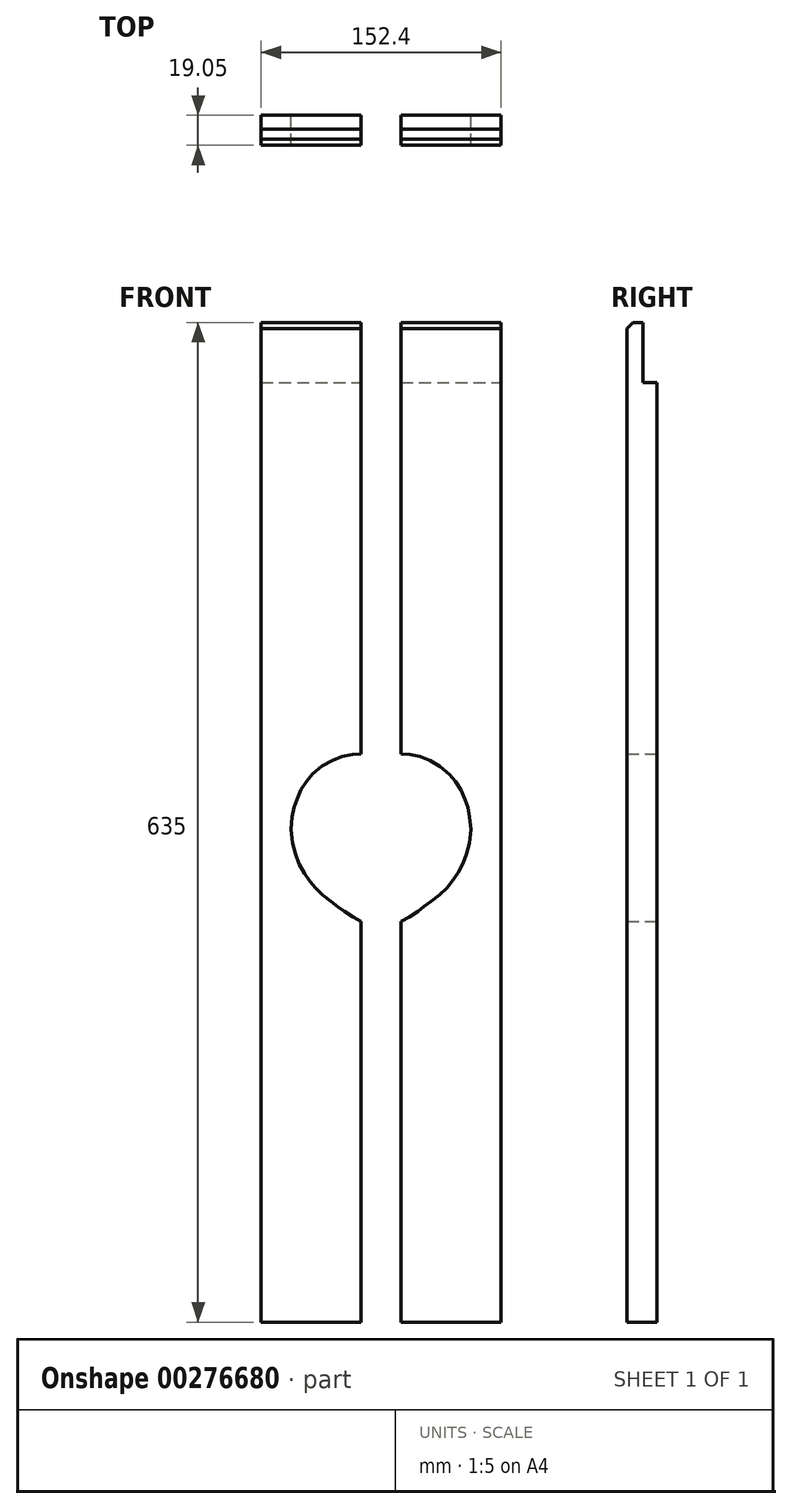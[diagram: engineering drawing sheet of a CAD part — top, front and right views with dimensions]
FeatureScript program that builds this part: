
annotation { "Feature Type Name" : "Feature", "Feature Type Description" : "" }
export const myFeature = defineFeature(function(context is Context, id is Id, definition is map)
    precondition{}
    {
        {
            var Q0;
            Q0=qCreatedBy(makeId("Front.planeOp"),FACE);
            var sketch = newSketch(context, id + "F0", { "sketchPlane" : qUnion([Q0])});
            skLineSegment(sketch, "E0.bottom", {"start": v(0, 0) * mm, "end": v(63.5, 0) * mm});
            skLineSegment(sketch, "E0.top", {"start": v(0, 635) * mm, "end": v(63.5, 635) * mm});
            skLineSegment(sketch, "E0.left", {"start": v(0, 0) * mm, "end": v(0, 635) * mm});
            skLineSegment(sketch, "E0.right", {"start": v(63.5, 0) * mm, "end": v(63.5, 635) * mm});
            skLineSegment(sketch, "E1.bottom", {"start": v(88.9, 0) * mm, "end": v(152.4, 0) * mm});
            skLineSegment(sketch, "E1.top", {"start": v(88.9, 635) * mm, "end": v(152.4, 635) * mm});
            skLineSegment(sketch, "E1.left", {"start": v(88.9, 0) * mm, "end": v(88.9, 635) * mm});
            skLineSegment(sketch, "E1.right", {"start": v(152.4, 0) * mm, "end": v(152.4, 635) * mm});
            skSolve(sketch);
        }
        {
            var Q0;
            Q0=makeQuery(id+"F0.imprint","IMPRINT",FACE,{"disambiguationData":[TD([[makeQuery(id+"F0.imprint","IMPRINT",EDGE,{"derivedFrom":sQuery(id+"F0.wireOp",EDGE,"E0.bottom")}),1.0]])]});
            extrude(context, id + "F1", {"entities" : qUnion([Q0]), "depth" : 19.05 * mm, "offsetDistance" : 25.4 * mm});
        }
        {
            var Q0;
            Q0 = qSketchRegion(id + "F0", true);
            extrude(context, id + "F2", {"entities" : qUnion([Q0]), "operationType" : NewBodyOperationType.ADD, "depth" : 19.05 * mm, "offsetDistance" : 25.4 * mm});
        }
        {
            var Q0;
            Q0=qCreatedBy(makeId("Front.planeOp"),FACE);
            var sketch = newSketch(context, id + "F3", { "sketchPlane" : qUnion([Q0])});
            skFitSpline(sketch, "E2", {"points": [v(72.78, 256.94) * mm, v(84.86, 261.1) * mm, v(98.45, 269.65) * mm, v(113.58, 282.58) * mm, v(122.79, 298.59) * mm, v(125.42, 312.18) * mm, v(123.66, 325.55) * mm, v(117.09, 339.37) * mm, v(103.93, 349.88) * mm, v(90.12, 353.2) * mm, v(79.16, 351.2) * mm, v(76.1, 348.98) * mm], "startDerivative": vector(114.3, 25.95) * mm, "endDerivative": vector(-50.63, -47.67) * mm});
            skFitSpline(sketch, "E3.MirrorCS", {"points": [v(79.42, 256.94) * mm, v(67.34, 261.1) * mm, v(53.75, 269.65) * mm, v(38.62, 282.58) * mm, v(29.41, 298.59) * mm, v(26.78, 312.18) * mm, v(28.54, 325.55) * mm, v(35.12, 339.37) * mm, v(48.27, 349.88) * mm, v(62.09, 353.2) * mm, v(73.04, 351.2) * mm, v(76.1, 348.98) * mm], "startDerivative": vector(-114.3, 25.95) * mm, "endDerivative": vector(50.63, -47.67) * mm});
            skFitSpline(sketch, "E4.0", {"points": [v(77.73, 249.51) * mm, v(77.04, 249.67) * mm, v(75.6, 250.02) * mm, v(73.27, 250.68) * mm, v(70.8, 251.47) * mm, v(68.25, 252.4) * mm, v(66.09, 253.3) * mm, v(64.34, 254.08) * mm, v(62.61, 254.92) * mm, v(60.53, 256.03) * mm, v(58.12, 257.45) * mm, v(55.8, 258.93) * mm, v(53.52, 260.46) * mm, v(51.66, 261.77) * mm, v(50.17, 262.84) * mm, v(49.06, 263.64) * mm, v(47.92, 264.46) * mm, v(46.38, 265.59) * mm, v(44.4, 267.06) * mm, v(42, 268.94) * mm, v(39.57, 270.94) * mm, v(37.18, 273.09) * mm, v(35.23, 275) * mm, v(33.71, 276.62) * mm, v(32.6, 277.88) * mm, v(31.54, 279.18) * mm, v(30.19, 280.93) * mm, v(28.62, 283.17) * mm, v(26.92, 285.92) * mm, v(25.4, 288.7) * mm, v(24.05, 291.49) * mm, v(22.87, 294.27) * mm, v(21.86, 297.03) * mm, v(21, 299.77) * mm, v(20.08, 303.43) * mm, v(19.32, 308) * mm, v(19.05, 313.47) * mm, v(19.34, 318) * mm, v(19.85, 321.61) * mm, v(20.37, 324.3) * mm, v(20.9, 326.52) * mm, v(21.39, 328.29) * mm, v(21.92, 330.08) * mm, v(22.68, 332.34) * mm, v(23.78, 335.06) * mm, v(25.07, 337.79) * mm, v(26.59, 340.48) * mm, v(28.06, 342.68) * mm, v(29.37, 344.4) * mm, v(30.75, 346.06) * mm, v(32.6, 348.03) * mm, v(35.74, 350.92) * mm, v(39.15, 353.46) * mm, v(42.72, 355.61) * mm, v(45.46, 357.03) * mm, v(48.26, 358.23) * mm, v(51.11, 359.22) * mm, v(54.01, 359.98) * mm, v(56.96, 360.51) * mm, v(59.44, 360.75) * mm, v(61.43, 360.83) * mm, v(63.43, 360.83) * mm, v(65.89, 360.68) * mm, v(68.73, 360.32) * mm, v(70.98, 359.86) * mm, v(72.7, 359.41) * mm, v(73.96, 359.02) * mm, v(74.99, 358.65) * mm, v(75.8, 358.32) * mm, v(76.4, 358.04) * mm, v(77, 357.74) * mm, v(77.75, 357.33) * mm, v(78.62, 356.78) * mm, v(79.53, 356.12) * mm, v(80.3, 355.49) * mm, v(80.9, 354.94) * mm, v(81.2, 354.65) * mm, v(81.33, 354.53) * mm]});
            skFitSpline(sketch, "E4.1", {"points": [v(74.47, 249.51) * mm, v(75.16, 249.67) * mm, v(76.6, 250.02) * mm, v(78.93, 250.68) * mm, v(81.4, 251.47) * mm, v(83.95, 252.4) * mm, v(86.12, 253.3) * mm, v(87.86, 254.08) * mm, v(89.59, 254.92) * mm, v(91.67, 256.03) * mm, v(94.08, 257.45) * mm, v(96.4, 258.93) * mm, v(98.68, 260.46) * mm, v(100.54, 261.77) * mm, v(102.03, 262.84) * mm, v(103.15, 263.64) * mm, v(104.28, 264.46) * mm, v(105.83, 265.59) * mm, v(107.8, 267.06) * mm, v(110.21, 268.94) * mm, v(112.63, 270.94) * mm, v(115.02, 273.09) * mm, v(116.97, 275) * mm, v(118.49, 276.62) * mm, v(119.6, 277.88) * mm, v(120.66, 279.18) * mm, v(122.01, 280.93) * mm, v(123.59, 283.17) * mm, v(125.28, 285.92) * mm, v(126.8, 288.7) * mm, v(128.15, 291.49) * mm, v(129.33, 294.27) * mm, v(130.34, 297.03) * mm, v(131.2, 299.77) * mm, v(132.12, 303.43) * mm, v(132.88, 308) * mm, v(133.15, 313.47) * mm, v(132.86, 318) * mm, v(132.35, 321.61) * mm, v(131.84, 324.3) * mm, v(131.3, 326.52) * mm, v(130.82, 328.29) * mm, v(130.28, 330.08) * mm, v(129.52, 332.34) * mm, v(128.43, 335.06) * mm, v(127.13, 337.79) * mm, v(125.61, 340.48) * mm, v(124.15, 342.68) * mm, v(122.83, 344.4) * mm, v(121.45, 346.06) * mm, v(119.61, 348.03) * mm, v(116.46, 350.92) * mm, v(113.06, 353.46) * mm, v(109.49, 355.61) * mm, v(106.74, 357.03) * mm, v(103.95, 358.23) * mm, v(101.1, 359.22) * mm, v(98.19, 359.98) * mm, v(95.24, 360.51) * mm, v(92.76, 360.75) * mm, v(90.77, 360.83) * mm, v(88.77, 360.83) * mm, v(86.31, 360.68) * mm, v(83.47, 360.32) * mm, v(81.22, 359.86) * mm, v(79.5, 359.41) * mm, v(78.24, 359.02) * mm, v(77.22, 358.65) * mm, v(76.4, 358.32) * mm, v(75.8, 358.04) * mm, v(75.2, 357.74) * mm, v(74.45, 357.33) * mm, v(73.58, 356.78) * mm, v(72.67, 356.12) * mm, v(71.91, 355.49) * mm, v(71.3, 354.94) * mm, v(71, 354.65) * mm, v(70.87, 354.53) * mm]});
            skSolve(sketch);
        }
        {
            var Q0;
            Q0 = qSketchRegion(id + "F3", true);
            var Q1;
            {var subQ0=sQuery(id+"F3.wireOp",EDGE,"E3.MirrorCS");var subQ1=sQuery(id+"F3.wireOp",EDGE,"E2");var subQ2=makeQuery(id+"F3.imprint","INTERSECT",VERTEX,{"disambiguationData":[OD(0.0)],"derivedFrom":[subQ1,subQ0]});Q1=makeQuery(id+"F3.imprint","IMPRINT",FACE,{"disambiguationData":[TD([[makeQuery(id+"F3.imprint","IMPRINT",EDGE,{"disambiguationData":[TD([[subQ2,-1.0]])],"derivedFrom":subQ1}),1.0]])]});}
            extrude(context, id + "F4", {"entities" : qUnion([Q0, Q1]), "operationType" : NewBodyOperationType.REMOVE, "depth" : 25.4 * mm, "offsetDistance" : 25.4 * mm});
        }
        {
            var Q0;
            Q0=makeQuery(id+"F2.opExtrude","SWEPT_FACE",FACE,{"disambiguationData":[OSD([sQuery(id+"F0.wireOp",EDGE,"E1.right")])]});
            var sketch = newSketch(context, id + "F5", { "sketchPlane" : qUnion([Q0])});
            skLineSegment(sketch, "E5", {"start": v(-8.9, 635) * mm, "end": v(-8.9, 596.9) * mm});
            skLineSegment(sketch, "E6", {"start": v(-8.9, 596.9) * mm, "end": v(0, 596.9) * mm});
            skLineSegment(sketch, "E7", {"start": v(-15.24, 635) * mm, "end": v(-19.05, 631.2) * mm});
            skSolve(sketch);
        }
        {
            var Q0;
            {var subQ0=sQuery(id+"F5.wireOp",EDGE,"E7");Q0=makeQuery(id+"F5.imprint","IMPRINT",FACE,{"disambiguationData":[TD([[makeQuery(id+"F5.imprint","IMPRINT",EDGE,{"derivedFrom":subQ0}),-1.0]])]});}
            var Q1;
            {var subQ0=sQuery(id+"F5.wireOp",EDGE,"E5");Q1=makeQuery(id+"F5.imprint","IMPRINT",FACE,{"disambiguationData":[TD([[makeQuery(id+"F5.imprint","IMPRINT",EDGE,{"derivedFrom":subQ0}),1.0]])]});}
            extrude(context, id + "F6", {"entities" : qUnion([Q0, Q1]), "operationType" : NewBodyOperationType.REMOVE, "oppositeDirection" : true, "depth" : 203.2 * mm, "offsetDistance" : 25.4 * mm});
        }
    });
